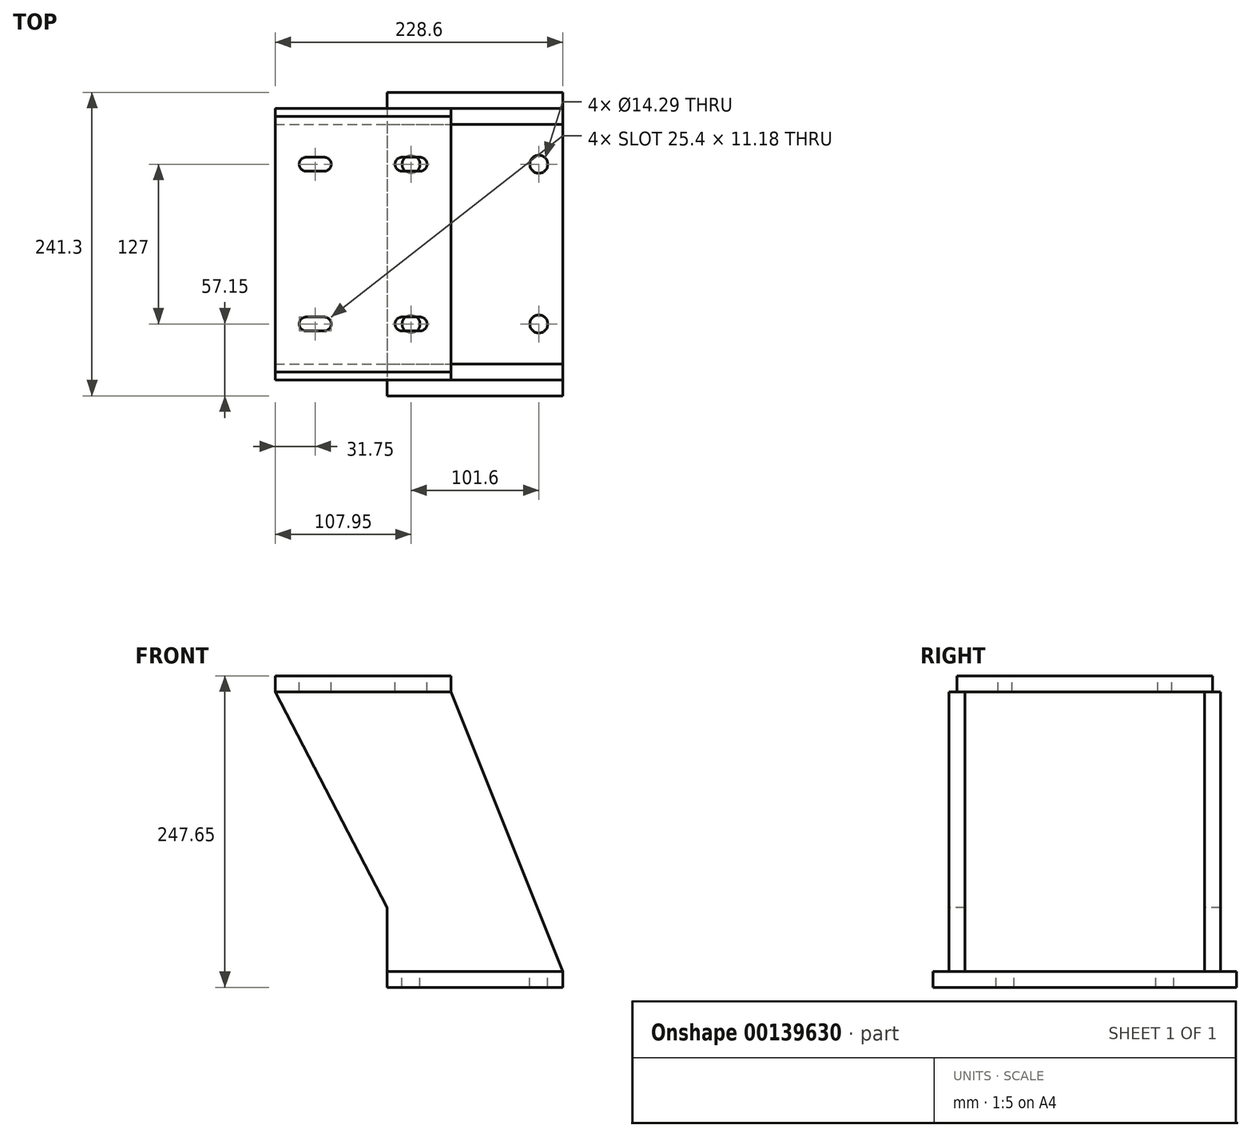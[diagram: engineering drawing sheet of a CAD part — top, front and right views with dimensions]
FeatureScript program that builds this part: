
annotation { "Feature Type Name" : "Feature", "Feature Type Description" : "" }
export const myFeature = defineFeature(function(context is Context, id is Id, definition is map)
    precondition{}
    {
        {
            var Q0;
            Q0=qCreatedBy(makeId("Top.planeOp"),FACE);
            var sketch = newSketch(context, id + "F0", { "sketchPlane" : qUnion([Q0])});
            skLineSegment(sketch, "E0.bottom", {"start": v(-69.85, 120.65) * mm, "end": v(69.85, 120.65) * mm});
            skLineSegment(sketch, "E0.top", {"start": v(-69.85, -120.65) * mm, "end": v(69.85, -120.65) * mm});
            skLineSegment(sketch, "E0.left", {"start": v(-69.85, 120.65) * mm, "end": v(-69.85, -120.65) * mm});
            skLineSegment(sketch, "E0.right", {"start": v(69.85, 120.65) * mm, "end": v(69.85, -120.65) * mm});
            skPoint(sketch, "E0.middle", {"position": v(0, 0) * mm});
            skSolve(sketch);
        }
        {
            var Q0;
            Q0 = qSketchRegion(id + "F0", true);
            extrude(context, id + "F1", {"entities" : qUnion([Q0]), "depth" : 12.7 * mm});
        }
        {
            var Q0;
            Q0=makeQuery(id+"F1.opExtrude","CAP_FACE",FACE,{"disambiguationData":[OSD([sQuery(id+"F0.wireOp",EDGE,"E0.bottom"),sQuery(id+"F0.wireOp",EDGE,"E0.top"),sQuery(id+"F0.wireOp",EDGE,"E0.left"),sQuery(id+"F0.wireOp",EDGE,"E0.right")])],"isStart":false});
            var sketch = newSketch(context, id + "F2", { "sketchPlane" : qUnion([Q0])});
            skLineSegment(sketch, "E1", {"start": v(-131.08, 0) * mm, "end": v(105.17, 0) * mm, "construction": true});
            skLineSegment(sketch, "E2.0", {"start": v(69.85, 120.65) * mm, "end": v(69.85, -120.65) * mm, "construction": true});
            skLineSegment(sketch, "E3.0", {"start": v(50.8, 120.65) * mm, "end": v(50.8, -120.65) * mm, "construction": true});
            skLineSegment(sketch, "E4.0", {"start": v(-50.8, 120.65) * mm, "end": v(-50.8, -120.65) * mm, "construction": true});
            skLineSegment(sketch, "E5.0", {"start": v(-131.08, -63.5) * mm, "end": v(105.17, -63.5) * mm, "construction": true});
            skPoint(sketch, "E6", {"position": v(-50.8, -63.5) * mm});
            skPoint(sketch, "E7", {"position": v(50.8, -63.5) * mm});
            skPoint(sketch, "E8.MirrorP", {"position": v(-50.8, 63.5) * mm});
            skPoint(sketch, "E9.MirrorP", {"position": v(50.8, 63.5) * mm});
            skSolve(sketch);
        }
        {
            var Q0;
            Q0=sQuery(id+"F2.wireOp",VERTEX,"E8.MirrorP");
            var Q1;
            Q1=sQuery(id+"F2.wireOp",VERTEX,"E9.MirrorP");
            var Q2;
            Q2=sQuery(id+"F2.wireOp",VERTEX,"E7");
            var Q3;
            Q3=sQuery(id+"F2.wireOp",VERTEX,"E6");
            var Q4;
            Q4=makeQuery(id+"F1.opExtrude","SWEPT_BODY",BODY,{"disambiguationData":[OSD([sQuery(id+"F0.wireOp",EDGE,"E0.bottom"),sQuery(id+"F0.wireOp",EDGE,"E0.top"),sQuery(id+"F0.wireOp",EDGE,"E0.left"),sQuery(id+"F0.wireOp",EDGE,"E0.right")])]});
            hole(context, id + "F3", {"style" : HoleStyle.SIMPLE, "endStyle" : HoleEndStyle.THROUGH, "holeDiameter" : 14.29 * mm, "locations" : qUnion([Q0, Q1, Q2, Q3]), "scope" : qUnion([Q4]), "isTappedThrough" : true});
        }
        {
            var Q0;
            Q0=makeQuery(id+"F1.opExtrude","CAP_FACE",FACE,{"disambiguationData":[OSD([sQuery(id+"F0.wireOp",EDGE,"E0.bottom"),sQuery(id+"F0.wireOp",EDGE,"E0.top"),sQuery(id+"F0.wireOp",EDGE,"E0.left"),sQuery(id+"F0.wireOp",EDGE,"E0.right")])],"isStart":false});
            var sketch = newSketch(context, id + "F4", { "sketchPlane" : qUnion([Q0])});
            skLineSegment(sketch, "E10", {"start": v(-175.8, 0) * mm, "end": v(168.17, 0) * mm, "construction": true});
            skLineSegment(sketch, "E11.0", {"start": v(69.85, 120.65) * mm, "end": v(69.85, -120.65) * mm, "construction": true});
            skLineSegment(sketch, "E12.0", {"start": v(-158.75, 120.65) * mm, "end": v(-158.75, -120.65) * mm, "construction": true});
            skLineSegment(sketch, "E13.bottom", {"start": v(-158.75, -95.25) * mm, "end": v(69.85, -95.25) * mm});
            skLineSegment(sketch, "E13.top", {"start": v(-158.75, -107.95) * mm, "end": v(69.85, -107.95) * mm});
            skLineSegment(sketch, "E13.left", {"start": v(-158.75, -95.25) * mm, "end": v(-158.75, -107.95) * mm});
            skLineSegment(sketch, "E13.right", {"start": v(69.85, -95.25) * mm, "end": v(69.85, -107.95) * mm});
            skLineSegment(sketch, "E14.MirrorCS", {"start": v(-158.75, 95.25) * mm, "end": v(-158.75, 107.95) * mm});
            skLineSegment(sketch, "E15.MirrorCS", {"start": v(69.85, 95.25) * mm, "end": v(69.85, 107.95) * mm});
            skLineSegment(sketch, "E16.MirrorCS", {"start": v(-158.75, 107.95) * mm, "end": v(69.85, 107.95) * mm});
            skLineSegment(sketch, "E17.MirrorCS", {"start": v(-158.75, 95.25) * mm, "end": v(69.85, 95.25) * mm});
            skSolve(sketch);
        }
        {
            var Q0;
            Q0 = qSketchRegion(id + "F4", true);
            extrude(context, id + "F5", {"entities" : qUnion([Q0]), "operationType" : NewBodyOperationType.ADD, "depth" : 222.25 * mm});
        }
        {
            var Q0;
            Q0=makeQuery(id+"F5.opExtrude","SWEPT_FACE",FACE,{"disambiguationData":[OSD([sQuery(id+"F4.wireOp",EDGE,"E13.top")])]});
            var sketch = newSketch(context, id + "F6", { "sketchPlane" : qUnion([Q0])});
            skLineSegment(sketch, "E18", {"start": v(-69.85, 12.7) * mm, "end": v(-69.85, 63.5) * mm});
            skLineSegment(sketch, "E19", {"start": v(-69.85, 63.5) * mm, "end": v(-158.75, 234.95) * mm});
            skLineSegment(sketch, "E20", {"start": v(-158.75, 234.95) * mm, "end": v(-158.75, 12.7) * mm});
            skLineSegment(sketch, "E21", {"start": v(-158.75, 12.7) * mm, "end": v(-69.85, 12.7) * mm});
            skSolve(sketch);
        }
        {
            var Q0;
            Q0 = qSketchRegion(id + "F6", true);
            extrude(context, id + "F7", {"entities" : qUnion([Q0]), "operationType" : NewBodyOperationType.REMOVE, "endBound" : BoundingType.THROUGH_ALL, "oppositeDirection" : true, "depth" : 25.4 * mm});
        }
        {
            var Q0;
            Q0=makeQuery(id+"F5.opExtrude","SWEPT_FACE",FACE,{"disambiguationData":[OSD([sQuery(id+"F4.wireOp",EDGE,"E13.top")])]});
            var sketch = newSketch(context, id + "F8", { "sketchPlane" : qUnion([Q0])});
            skLineSegment(sketch, "E22", {"start": v(-158.75, 234.95) * mm, "end": v(-19.05, 234.95) * mm, "construction": true});
            skLineSegment(sketch, "E23", {"start": v(-19.05, 234.95) * mm, "end": v(69.85, 12.7) * mm});
            skLineSegment(sketch, "E24", {"start": v(69.85, 12.7) * mm, "end": v(69.85, 234.95) * mm});
            skLineSegment(sketch, "E25", {"start": v(69.85, 234.95) * mm, "end": v(-19.05, 234.95) * mm});
            skSolve(sketch);
        }
        {
            var Q0;
            Q0 = qSketchRegion(id + "F8", true);
            extrude(context, id + "F9", {"entities" : qUnion([Q0]), "operationType" : NewBodyOperationType.REMOVE, "endBound" : BoundingType.THROUGH_ALL, "oppositeDirection" : true, "depth" : 25.4 * mm});
        }
        {
            var Q0;
            Q0=makeQuery(id+"F5.opExtrude","CAP_FACE",FACE,{"disambiguationData":[OSD([sQuery(id+"F4.wireOp",EDGE,"E13.bottom"),sQuery(id+"F4.wireOp",EDGE,"E13.top"),sQuery(id+"F4.wireOp",EDGE,"E13.left"),sQuery(id+"F4.wireOp",EDGE,"E13.right")])],"isStart":false});
            var sketch = newSketch(context, id + "F10", { "sketchPlane" : qUnion([Q0])});
            skLineSegment(sketch, "E26", {"start": v(-210.42, 0) * mm, "end": v(158.02, 0) * mm, "construction": true});
            skLineSegment(sketch, "E27.0", {"start": v(-158.75, -101.6) * mm, "end": v(-19.05, -101.6) * mm});
            skLineSegment(sketch, "E28.0", {"start": v(-158.75, 101.6) * mm, "end": v(-158.75, -101.6) * mm});
            skLineSegment(sketch, "E29.0", {"start": v(-19.05, 101.6) * mm, "end": v(-19.05, -101.6) * mm});
            skLineSegment(sketch, "E30.MirrorCS", {"start": v(-158.75, 101.6) * mm, "end": v(-14.71, 101.6) * mm});
            skPoint(sketch, "E31.orphan", {"position": v(-210.42, -101.6) * mm});
            skPoint(sketch, "E32.orphan", {"position": v(158.02, -101.6) * mm});
            skPoint(sketch, "E33.orphan", {"position": v(-19.05, -107.95) * mm});
            skPoint(sketch, "E34.orphan", {"position": v(-158.75, -107.95) * mm});
            skPoint(sketch, "E35.orphan", {"position": v(-158.75, -95.25) * mm});
            skPoint(sketch, "E36.orphan", {"position": v(-19.05, -95.25) * mm});
            skPoint(sketch, "E37.orphan", {"position": v(158.02, 101.6) * mm});
            skPoint(sketch, "E38.orphan", {"position": v(-210.42, 101.6) * mm});
            skSolve(sketch);
        }
        {
            var Q0;
            Q0 = qSketchRegion(id + "F10", true);
            extrude(context, id + "F11", {"entities" : qUnion([Q0]), "operationType" : NewBodyOperationType.ADD, "depth" : 12.7 * mm});
        }
        {
            var Q0;
            Q0=makeQuery(id+"F11.opExtrude","CAP_FACE",FACE,{"disambiguationData":[OSD([sQuery(id+"F10.wireOp",EDGE,"E27.0"),sQuery(id+"F10.wireOp",EDGE,"E28.0"),sQuery(id+"F10.wireOp",EDGE,"E29.0"),sQuery(id+"F10.wireOp",EDGE,"E30.MirrorCS")])],"isStart":false});
            var sketch = newSketch(context, id + "F12", { "sketchPlane" : qUnion([Q0])});
            skLineSegment(sketch, "E39", {"start": v(-240.2, 0) * mm, "end": v(151.34, 0) * mm, "construction": true});
            skLineSegment(sketch, "E40.0", {"start": v(-158.75, 101.6) * mm, "end": v(-158.75, -101.6) * mm, "construction": true});
            skLineSegment(sketch, "E41.0", {"start": v(-88.9, 101.6) * mm, "end": v(-88.9, -101.6) * mm, "construction": true});
            skLineSegment(sketch, "E42.0", {"start": v(-240.2, 63.5) * mm, "end": v(151.34, 63.5) * mm, "construction": true});
            skLineSegment(sketch, "E43.0", {"start": v(-127, 101.6) * mm, "end": v(-127, -101.6) * mm, "construction": true});
            skLineSegment(sketch, "E44.0", {"start": v(-134.11, 101.6) * mm, "end": v(-134.11, -101.6) * mm, "construction": true});
            skLineSegment(sketch, "E45.0", {"start": v(-119.89, 101.6) * mm, "end": v(-119.89, -101.6) * mm, "construction": true});
            skLineSegment(sketch, "E46", {"start": v(-134.11, 63.5) * mm, "end": v(-119.89, 63.5) * mm});
            skLineSegment(sketch, "E47.MirrorCS", {"start": v(-134.11, -63.5) * mm, "end": v(-119.89, -63.5) * mm});
            skArc(sketch, "E48.0.startCap", {"start": v(-134.11, -69.09) * mm, "mid": v(-139.7, -63.5) * mm, "end": v(-134.11, -57.91) * mm});
            skArc(sketch, "E48.0.endCap", {"start": v(-119.89, -57.91) * mm, "mid": v(-114.3, -63.5) * mm, "end": v(-119.89, -69.09) * mm});
            skLineSegment(sketch, "E48.0.left", {"start": v(-134.11, -57.91) * mm, "end": v(-119.89, -57.91) * mm});
            skLineSegment(sketch, "E48.0.right", {"start": v(-134.11, -69.09) * mm, "end": v(-119.89, -69.09) * mm});
            skLineSegment(sketch, "E49.MirrorCS", {"start": v(-43.69, -63.5) * mm, "end": v(-57.91, -63.5) * mm});
            skArc(sketch, "E50.MirrorCS", {"start": v(-43.69, -69.09) * mm, "mid": v(-38.1, -63.5) * mm, "end": v(-43.69, -57.91) * mm});
            skArc(sketch, "E51.MirrorCS", {"start": v(-57.91, -57.91) * mm, "mid": v(-63.5, -63.5) * mm, "end": v(-57.91, -69.09) * mm});
            skLineSegment(sketch, "E52.MirrorCS", {"start": v(-43.69, -69.09) * mm, "end": v(-57.91, -69.09) * mm});
            skLineSegment(sketch, "E53.MirrorCS", {"start": v(-43.69, -57.91) * mm, "end": v(-57.91, -57.91) * mm});
            skLineSegment(sketch, "E54.MirrorCS", {"start": v(-43.69, 57.91) * mm, "end": v(-57.91, 57.91) * mm});
            skLineSegment(sketch, "E55.MirrorCS", {"start": v(-134.11, 69.09) * mm, "end": v(-119.89, 69.09) * mm});
            skLineSegment(sketch, "E56.MirrorCS", {"start": v(-43.69, 69.09) * mm, "end": v(-57.91, 69.09) * mm});
            skLineSegment(sketch, "E57.MirrorCS", {"start": v(-134.11, 57.91) * mm, "end": v(-119.89, 57.91) * mm});
            skArc(sketch, "E58.MirrorCS", {"start": v(-119.89, 57.91) * mm, "mid": v(-114.3, 63.5) * mm, "end": v(-119.89, 69.09) * mm});
            skArc(sketch, "E59.MirrorCS", {"start": v(-134.11, 69.09) * mm, "mid": v(-139.7, 63.5) * mm, "end": v(-134.11, 57.91) * mm});
            skArc(sketch, "E60.MirrorCS", {"start": v(-57.91, 57.91) * mm, "mid": v(-63.5, 63.5) * mm, "end": v(-57.91, 69.09) * mm});
            skLineSegment(sketch, "E61.MirrorCS", {"start": v(-43.69, 63.5) * mm, "end": v(-57.91, 63.5) * mm});
            skArc(sketch, "E62.MirrorCS", {"start": v(-43.69, 69.09) * mm, "mid": v(-38.1, 63.5) * mm, "end": v(-43.69, 57.91) * mm});
            skSolve(sketch);
        }
        {
            var Q0;
            Q0 = qSketchRegion(id + "F12", true);
            extrude(context, id + "F13", {"entities" : qUnion([Q0]), "operationType" : NewBodyOperationType.REMOVE, "oppositeDirection" : true, "depth" : 25.4 * mm});
        }
    });
